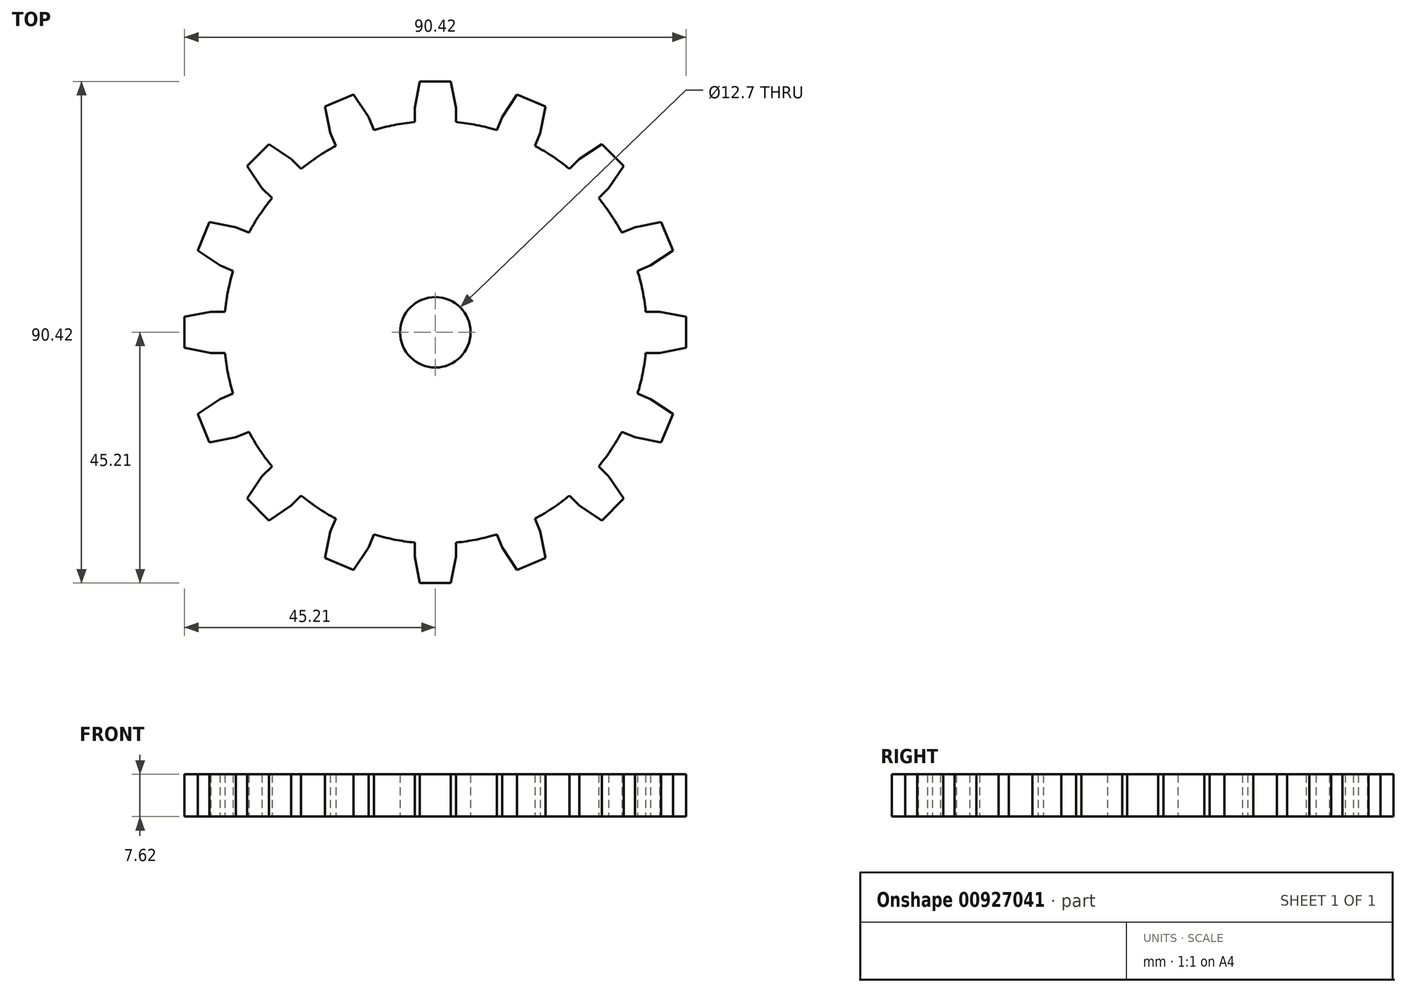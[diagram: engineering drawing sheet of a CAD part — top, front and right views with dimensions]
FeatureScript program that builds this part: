
annotation { "Feature Type Name" : "Feature", "Feature Type Description" : "" }
export const myFeature = defineFeature(function(context is Context, id is Id, definition is map)
    precondition{}
    {
        {
            var Q0;
            Q0=qCreatedBy(makeId("Top.planeOp"),FACE);
            var sketch = newSketch(context, id + "F0", { "sketchPlane" : qUnion([Q0])});
            skArc(sketch, "E0", {"start": v(-24.18, -29.44) * mm, "mid": v(-21.17, -31.68) * mm, "end": v(-17.95, -33.6) * mm});
            skLineSegment(sketch, "E1", {"start": v(0, 45.21) * mm, "end": v(2.8, 45.21) * mm});
            skLineSegment(sketch, "E2", {"start": v(2.8, 45.21) * mm, "end": v(3.72, 40.46) * mm});
            skLineSegment(sketch, "E3", {"start": v(3.72, 40.46) * mm, "end": v(3.72, 37.92) * mm});
            skLineSegment(sketch, "E4.MirrorCS", {"start": v(-2.8, 45.21) * mm, "end": v(-3.72, 40.46) * mm});
            skLineSegment(sketch, "E5.MirrorCS", {"start": v(-3.72, 40.46) * mm, "end": v(-3.72, 37.92) * mm});
            skLineSegment(sketch, "E6.MirrorCS", {"start": v(0, 45.21) * mm, "end": v(-2.8, 45.21) * mm});
            skLineSegment(sketch, "E7.1.0", {"start": v(-17.3, 41.77) * mm, "end": v(-19.88, 40.7) * mm});
            skLineSegment(sketch, "E7.1.1", {"start": v(-17.3, 41.77) * mm, "end": v(-14.72, 42.84) * mm});
            skLineSegment(sketch, "E7.1.2", {"start": v(-14.72, 42.84) * mm, "end": v(-12.05, 38.8) * mm});
            skLineSegment(sketch, "E7.1.3", {"start": v(-12.05, 38.8) * mm, "end": v(-11.07, 36.45) * mm});
            skLineSegment(sketch, "E7.1.4", {"start": v(-18.92, 35.96) * mm, "end": v(-17.95, 33.6) * mm});
            skLineSegment(sketch, "E7.1.5", {"start": v(-19.88, 40.7) * mm, "end": v(-18.92, 35.96) * mm});
            skLineSegment(sketch, "E7.2.0", {"start": v(-31.97, 31.97) * mm, "end": v(-33.95, 30) * mm});
            skLineSegment(sketch, "E7.2.1", {"start": v(-31.97, 31.97) * mm, "end": v(-30, 33.95) * mm});
            skLineSegment(sketch, "E7.2.2", {"start": v(-30, 33.95) * mm, "end": v(-25.98, 31.24) * mm});
            skLineSegment(sketch, "E7.2.3", {"start": v(-25.98, 31.24) * mm, "end": v(-24.18, 29.44) * mm});
            skLineSegment(sketch, "E7.2.4", {"start": v(-31.24, 25.98) * mm, "end": v(-29.44, 24.18) * mm});
            skLineSegment(sketch, "E7.2.5", {"start": v(-33.95, 30) * mm, "end": v(-31.24, 25.98) * mm});
            skLineSegment(sketch, "E7.3.0", {"start": v(-41.77, 17.3) * mm, "end": v(-42.84, 14.72) * mm});
            skLineSegment(sketch, "E7.3.1", {"start": v(-41.77, 17.3) * mm, "end": v(-40.7, 19.88) * mm});
            skLineSegment(sketch, "E7.3.2", {"start": v(-40.7, 19.88) * mm, "end": v(-35.96, 18.92) * mm});
            skLineSegment(sketch, "E7.3.3", {"start": v(-35.96, 18.92) * mm, "end": v(-33.6, 17.95) * mm});
            skLineSegment(sketch, "E7.3.4", {"start": v(-38.8, 12.05) * mm, "end": v(-36.45, 11.07) * mm});
            skLineSegment(sketch, "E7.3.5", {"start": v(-42.84, 14.72) * mm, "end": v(-38.8, 12.05) * mm});
            skLineSegment(sketch, "E7.4.0", {"start": v(-45.21, 0) * mm, "end": v(-45.21, -2.8) * mm});
            skLineSegment(sketch, "E7.4.1", {"start": v(-45.21, 0) * mm, "end": v(-45.21, 2.8) * mm});
            skLineSegment(sketch, "E7.4.2", {"start": v(-45.21, 2.8) * mm, "end": v(-40.46, 3.72) * mm});
            skLineSegment(sketch, "E7.4.3", {"start": v(-40.46, 3.72) * mm, "end": v(-37.92, 3.72) * mm});
            skLineSegment(sketch, "E7.4.4", {"start": v(-40.46, -3.72) * mm, "end": v(-37.92, -3.72) * mm});
            skLineSegment(sketch, "E7.4.5", {"start": v(-45.21, -2.8) * mm, "end": v(-40.46, -3.72) * mm});
            skLineSegment(sketch, "E7.5.0", {"start": v(-41.77, -17.3) * mm, "end": v(-40.7, -19.88) * mm});
            skLineSegment(sketch, "E7.5.1", {"start": v(-41.77, -17.3) * mm, "end": v(-42.84, -14.72) * mm});
            skLineSegment(sketch, "E7.5.2", {"start": v(-42.84, -14.72) * mm, "end": v(-38.8, -12.05) * mm});
            skLineSegment(sketch, "E7.5.3", {"start": v(-38.8, -12.05) * mm, "end": v(-36.45, -11.07) * mm});
            skLineSegment(sketch, "E7.5.4", {"start": v(-35.96, -18.92) * mm, "end": v(-33.6, -17.95) * mm});
            skLineSegment(sketch, "E7.5.5", {"start": v(-40.7, -19.88) * mm, "end": v(-35.96, -18.92) * mm});
            skLineSegment(sketch, "E7.6.0", {"start": v(-31.97, -31.97) * mm, "end": v(-30, -33.95) * mm});
            skLineSegment(sketch, "E7.6.1", {"start": v(-31.97, -31.97) * mm, "end": v(-33.95, -30) * mm});
            skLineSegment(sketch, "E7.6.2", {"start": v(-33.95, -30) * mm, "end": v(-31.24, -25.98) * mm});
            skLineSegment(sketch, "E7.6.3", {"start": v(-31.24, -25.98) * mm, "end": v(-29.44, -24.18) * mm});
            skLineSegment(sketch, "E7.6.4", {"start": v(-25.98, -31.24) * mm, "end": v(-24.18, -29.44) * mm});
            skLineSegment(sketch, "E7.6.5", {"start": v(-30, -33.95) * mm, "end": v(-25.98, -31.24) * mm});
            skLineSegment(sketch, "E7.7.0", {"start": v(-17.3, -41.77) * mm, "end": v(-14.72, -42.84) * mm});
            skLineSegment(sketch, "E7.7.1", {"start": v(-17.3, -41.77) * mm, "end": v(-19.88, -40.7) * mm});
            skLineSegment(sketch, "E7.7.2", {"start": v(-19.88, -40.7) * mm, "end": v(-18.92, -35.96) * mm});
            skLineSegment(sketch, "E7.7.3", {"start": v(-18.92, -35.96) * mm, "end": v(-17.95, -33.6) * mm});
            skLineSegment(sketch, "E7.7.4", {"start": v(-12.05, -38.8) * mm, "end": v(-11.07, -36.45) * mm});
            skLineSegment(sketch, "E7.7.5", {"start": v(-14.72, -42.84) * mm, "end": v(-12.05, -38.8) * mm});
            skLineSegment(sketch, "E7.8.0", {"start": v(0, -45.21) * mm, "end": v(2.8, -45.21) * mm});
            skLineSegment(sketch, "E7.8.1", {"start": v(0, -45.21) * mm, "end": v(-2.8, -45.21) * mm});
            skLineSegment(sketch, "E7.8.2", {"start": v(-2.8, -45.21) * mm, "end": v(-3.72, -40.46) * mm});
            skLineSegment(sketch, "E7.8.3", {"start": v(-3.72, -40.46) * mm, "end": v(-3.72, -37.92) * mm});
            skLineSegment(sketch, "E7.8.4", {"start": v(3.72, -40.46) * mm, "end": v(3.72, -37.92) * mm});
            skLineSegment(sketch, "E7.8.5", {"start": v(2.8, -45.21) * mm, "end": v(3.72, -40.46) * mm});
            skLineSegment(sketch, "E7.9.0", {"start": v(17.3, -41.77) * mm, "end": v(19.88, -40.7) * mm});
            skLineSegment(sketch, "E7.9.1", {"start": v(17.3, -41.77) * mm, "end": v(14.72, -42.84) * mm});
            skLineSegment(sketch, "E7.9.2", {"start": v(14.72, -42.84) * mm, "end": v(12.05, -38.8) * mm});
            skLineSegment(sketch, "E7.9.3", {"start": v(12.05, -38.8) * mm, "end": v(11.07, -36.45) * mm});
            skLineSegment(sketch, "E7.9.4", {"start": v(18.92, -35.96) * mm, "end": v(17.95, -33.6) * mm});
            skLineSegment(sketch, "E7.9.5", {"start": v(19.88, -40.7) * mm, "end": v(18.92, -35.96) * mm});
            skLineSegment(sketch, "E7.10.0", {"start": v(31.97, -31.97) * mm, "end": v(33.95, -30) * mm});
            skLineSegment(sketch, "E7.10.1", {"start": v(31.97, -31.97) * mm, "end": v(30, -33.95) * mm});
            skLineSegment(sketch, "E7.10.2", {"start": v(30, -33.95) * mm, "end": v(25.98, -31.24) * mm});
            skLineSegment(sketch, "E7.10.3", {"start": v(25.98, -31.24) * mm, "end": v(24.18, -29.44) * mm});
            skLineSegment(sketch, "E7.10.4", {"start": v(31.24, -25.98) * mm, "end": v(29.44, -24.18) * mm});
            skLineSegment(sketch, "E7.10.5", {"start": v(33.95, -30) * mm, "end": v(31.24, -25.98) * mm});
            skLineSegment(sketch, "E7.11.0", {"start": v(41.77, -17.3) * mm, "end": v(42.84, -14.72) * mm});
            skLineSegment(sketch, "E7.11.1", {"start": v(41.77, -17.3) * mm, "end": v(40.7, -19.88) * mm});
            skLineSegment(sketch, "E7.11.2", {"start": v(40.7, -19.88) * mm, "end": v(35.96, -18.92) * mm});
            skLineSegment(sketch, "E7.11.3", {"start": v(35.96, -18.92) * mm, "end": v(33.6, -17.95) * mm});
            skLineSegment(sketch, "E7.11.4", {"start": v(38.8, -12.05) * mm, "end": v(36.45, -11.07) * mm});
            skLineSegment(sketch, "E7.11.5", {"start": v(42.84, -14.72) * mm, "end": v(38.8, -12.05) * mm});
            skLineSegment(sketch, "E7.12.0", {"start": v(45.21, 0) * mm, "end": v(45.21, 2.8) * mm});
            skLineSegment(sketch, "E7.12.1", {"start": v(45.21, 0) * mm, "end": v(45.21, -2.8) * mm});
            skLineSegment(sketch, "E7.12.2", {"start": v(45.21, -2.8) * mm, "end": v(40.46, -3.72) * mm});
            skLineSegment(sketch, "E7.12.3", {"start": v(40.46, -3.72) * mm, "end": v(37.92, -3.72) * mm});
            skLineSegment(sketch, "E7.12.4", {"start": v(40.46, 3.72) * mm, "end": v(37.92, 3.72) * mm});
            skLineSegment(sketch, "E7.12.5", {"start": v(45.21, 2.8) * mm, "end": v(40.46, 3.72) * mm});
            skLineSegment(sketch, "E7.13.0", {"start": v(41.77, 17.3) * mm, "end": v(40.7, 19.88) * mm});
            skLineSegment(sketch, "E7.13.1", {"start": v(41.77, 17.3) * mm, "end": v(42.84, 14.72) * mm});
            skLineSegment(sketch, "E7.13.2", {"start": v(42.84, 14.72) * mm, "end": v(38.8, 12.05) * mm});
            skLineSegment(sketch, "E7.13.3", {"start": v(38.8, 12.05) * mm, "end": v(36.45, 11.07) * mm});
            skLineSegment(sketch, "E7.13.4", {"start": v(35.96, 18.92) * mm, "end": v(33.6, 17.95) * mm});
            skLineSegment(sketch, "E7.13.5", {"start": v(40.7, 19.88) * mm, "end": v(35.96, 18.92) * mm});
            skLineSegment(sketch, "E7.14.0", {"start": v(31.97, 31.97) * mm, "end": v(30, 33.95) * mm});
            skLineSegment(sketch, "E7.14.1", {"start": v(31.97, 31.97) * mm, "end": v(33.95, 30) * mm});
            skLineSegment(sketch, "E7.14.2", {"start": v(33.95, 30) * mm, "end": v(31.24, 25.98) * mm});
            skLineSegment(sketch, "E7.14.3", {"start": v(31.24, 25.98) * mm, "end": v(29.44, 24.18) * mm});
            skLineSegment(sketch, "E7.14.4", {"start": v(25.98, 31.24) * mm, "end": v(24.18, 29.44) * mm});
            skLineSegment(sketch, "E7.14.5", {"start": v(30, 33.95) * mm, "end": v(25.98, 31.24) * mm});
            skLineSegment(sketch, "E7.15.0", {"start": v(17.3, 41.77) * mm, "end": v(14.72, 42.84) * mm});
            skLineSegment(sketch, "E7.15.1", {"start": v(17.3, 41.77) * mm, "end": v(19.88, 40.7) * mm});
            skLineSegment(sketch, "E7.15.2", {"start": v(19.88, 40.7) * mm, "end": v(18.92, 35.96) * mm});
            skLineSegment(sketch, "E7.15.3", {"start": v(18.92, 35.96) * mm, "end": v(17.95, 33.6) * mm});
            skLineSegment(sketch, "E7.15.4", {"start": v(12.05, 38.8) * mm, "end": v(11.07, 36.45) * mm});
            skLineSegment(sketch, "E7.15.5", {"start": v(14.72, 42.84) * mm, "end": v(12.05, 38.8) * mm});
            skCircle(sketch, "E8", {"center": v(0, 0) * mm, "radius": 6.35 * mm});
            skArc(sketch, "E9.trimOffspring", {"start": v(-33.6, -17.95) * mm, "mid": v(-31.68, -21.17) * mm, "end": v(-29.44, -24.18) * mm});
            skArc(sketch, "E10.trimOffspring", {"start": v(-37.92, -3.72) * mm, "mid": v(-37.37, -7.43) * mm, "end": v(-36.45, -11.07) * mm});
            skArc(sketch, "E11.trimOffspring", {"start": v(-36.45, 11.07) * mm, "mid": v(-37.37, 7.43) * mm, "end": v(-37.92, 3.72) * mm});
            skArc(sketch, "E12.trimOffspring", {"start": v(-29.44, 24.18) * mm, "mid": v(-31.68, 21.17) * mm, "end": v(-33.6, 17.95) * mm});
            skArc(sketch, "E13.trimOffspring", {"start": v(-17.95, 33.6) * mm, "mid": v(-21.17, 31.68) * mm, "end": v(-24.18, 29.44) * mm});
            skArc(sketch, "E14.trimOffspring", {"start": v(-3.72, 37.92) * mm, "mid": v(-7.43, 37.37) * mm, "end": v(-11.07, 36.45) * mm});
            skArc(sketch, "E15.trimOffspring", {"start": v(11.07, 36.45) * mm, "mid": v(7.43, 37.37) * mm, "end": v(3.72, 37.92) * mm});
            skArc(sketch, "E16.trimOffspring", {"start": v(24.18, 29.44) * mm, "mid": v(21.17, 31.68) * mm, "end": v(17.95, 33.6) * mm});
            skArc(sketch, "E17.trimOffspring", {"start": v(-11.07, -36.45) * mm, "mid": v(-7.43, -37.37) * mm, "end": v(-3.72, -37.92) * mm});
            skArc(sketch, "E18.trimOffspring", {"start": v(3.72, -37.92) * mm, "mid": v(7.43, -37.37) * mm, "end": v(11.07, -36.45) * mm});
            skArc(sketch, "E19.trimOffspring", {"start": v(17.95, -33.6) * mm, "mid": v(21.17, -31.68) * mm, "end": v(24.18, -29.44) * mm});
            skArc(sketch, "E20.trimOffspring", {"start": v(29.44, -24.18) * mm, "mid": v(31.68, -21.17) * mm, "end": v(33.6, -17.95) * mm});
            skArc(sketch, "E21.trimOffspring", {"start": v(36.45, -11.07) * mm, "mid": v(37.37, -7.43) * mm, "end": v(37.92, -3.72) * mm});
            skArc(sketch, "E22.trimOffspring", {"start": v(37.92, 3.72) * mm, "mid": v(37.37, 7.43) * mm, "end": v(36.45, 11.07) * mm});
            skArc(sketch, "E23.trimOffspring", {"start": v(33.6, 17.95) * mm, "mid": v(31.68, 21.17) * mm, "end": v(29.44, 24.18) * mm});
            skSolve(sketch);
        }
        {
            var Q0;
            Q0=makeQuery(id+"F0.imprint","IMPRINT",FACE,{"disambiguationData":[TD([[makeQuery(id+"F0.imprint","IMPRINT",EDGE,{"derivedFrom":sQuery(id+"F0.wireOp",EDGE,"E1")}),-1.0]])]});
            extrude(context, id + "F1", {"entities" : qUnion([Q0]), "endBound" : BoundingType.SYMMETRIC, "depth" : 7.62 * mm, "offsetDistance" : 25.4 * mm});
        }
    });
